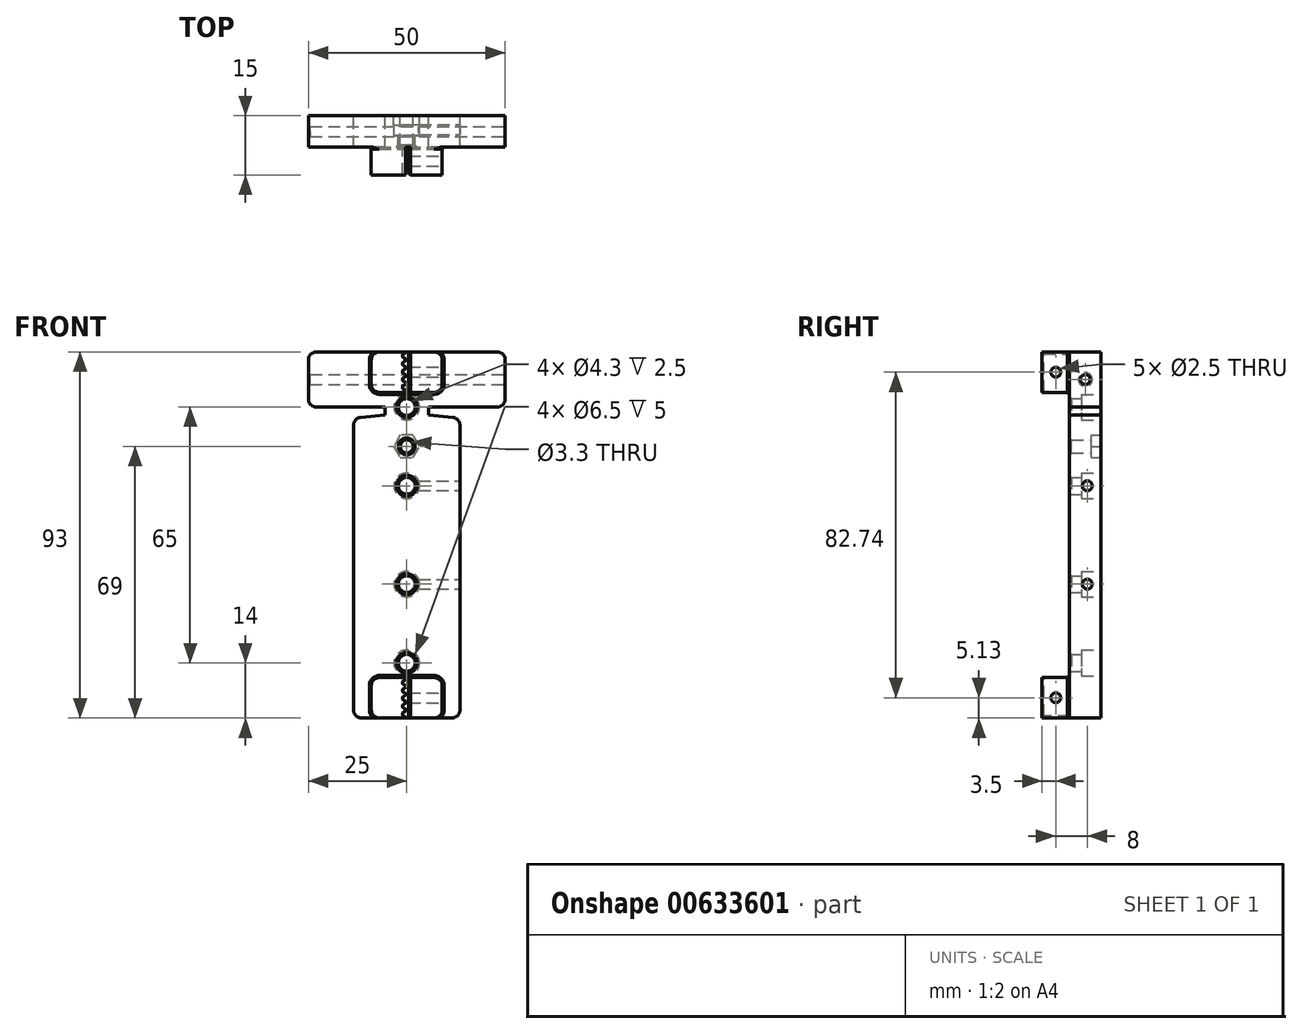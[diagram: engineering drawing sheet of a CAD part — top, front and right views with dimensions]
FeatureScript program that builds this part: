
annotation { "Feature Type Name" : "Feature", "Feature Type Description" : "" }
export const myFeature = defineFeature(function(context is Context, id is Id, definition is map)
    precondition{}
    {
        {
            var Q0;
            Q0=qCreatedBy(makeId("Front.planeOp"),FACE);
            var sketch = newSketch(context, id + "F0", { "sketchPlane" : qUnion([Q0])});
            skLineSegment(sketch, "E0.bottom", {"start": v(13.5, -86) * mm, "end": v(-13.5, -86) * mm});
            skLineSegment(sketch, "E0.left", {"start": v(13.5, -86) * mm, "end": v(13.5, -9.8) * mm});
            skLineSegment(sketch, "E0.right", {"start": v(-13.5, -86) * mm, "end": v(-13.5, -9.8) * mm});
            skLineSegment(sketch, "E1.top", {"start": v(-25, 7) * mm, "end": v(25, 7) * mm});
            skLineSegment(sketch, "E1.left", {"start": v(-25, -7) * mm, "end": v(-25, 7) * mm});
            skLineSegment(sketch, "E1.right", {"start": v(25, -7) * mm, "end": v(25, 7) * mm});
            skPoint(sketch, "E1.middle", {"position": v(0, 0) * mm});
            skCircle(sketch, "E2", {"center": v(0, -7) * mm, "radius": 2.15 * mm});
            skCircle(sketch, "E3", {"center": v(0, -17) * mm, "radius": 1.65 * mm});
            skCircle(sketch, "E4", {"center": v(0, -27) * mm, "radius": 2.15 * mm});
            skCircle(sketch, "E5", {"center": v(0, -52) * mm, "radius": 2.15 * mm});
            skCircle(sketch, "E6", {"center": v(0, -72) * mm, "radius": 2.15 * mm});
            skLineSegment(sketch, "E7", {"start": v(-32.04, -39.5) * mm, "end": v(39, -39.5) * mm, "construction": true});
            skLineSegment(sketch, "E8", {"start": v(-25, -7) * mm, "end": v(-13.5, -7) * mm});
            skLineSegment(sketch, "E9", {"start": v(13.5, -7) * mm, "end": v(25, -7) * mm});
            skLineSegment(sketch, "E10", {"start": v(0, 0) * mm, "end": v(0, -86) * mm, "construction": true});
            skLineSegment(sketch, "E11", {"start": v(-13.5, -7) * mm, "end": v(-5.5, -7) * mm});
            skLineSegment(sketch, "E12", {"start": v(-5.5, -7) * mm, "end": v(-5.5, -9) * mm});
            skLineSegment(sketch, "E13", {"start": v(-5.5, -9) * mm, "end": v(-13.5, -9.8) * mm});
            skLineSegment(sketch, "E14.MirrorCS", {"start": v(13.5, -7) * mm, "end": v(5.5, -7) * mm});
            skLineSegment(sketch, "E15.MirrorCS", {"start": v(5.5, -9) * mm, "end": v(13.5, -9.8) * mm});
            skLineSegment(sketch, "E16.MirrorCS", {"start": v(5.5, -7) * mm, "end": v(5.5, -9) * mm});
            skSolve(sketch);
        }
        {
            var Q0;
            Q0=makeQuery(id+"F0.imprint","IMPRINT",FACE,{"disambiguationData":[TD([[makeQuery(id+"F0.imprint","IMPRINT",EDGE,{"derivedFrom":sQuery(id+"F0.wireOp",EDGE,"E0.bottom")}),-1.0]])]});
            extrude(context, id + "F1", {"entities" : qUnion([Q0]), "endBound" : BoundingType.SYMMETRIC, "depth" : 8 * mm});
        }
        {
            var Q0;
            Q0=makeQuery(id+"F1.opExtrude","CAP_FACE",FACE,{"disambiguationData":[OSD([sQuery(id+"F0.wireOp",EDGE,"E0.bottom"),sQuery(id+"F0.wireOp",EDGE,"E0.left"),sQuery(id+"F0.wireOp",EDGE,"E0.right"),sQuery(id+"F0.wireOp",EDGE,"E1.top"),sQuery(id+"F0.wireOp",EDGE,"E1.left"),sQuery(id+"F0.wireOp",EDGE,"E1.right"),sQuery(id+"F0.wireOp",EDGE,"E2"),sQuery(id+"F0.wireOp",EDGE,"E3"),sQuery(id+"F0.wireOp",EDGE,"E4"),sQuery(id+"F0.wireOp",EDGE,"E5"),sQuery(id+"F0.wireOp",EDGE,"E6"),sQuery(id+"F0.wireOp",EDGE,"E8"),sQuery(id+"F0.wireOp",EDGE,"E9")])],"isStart":false});
            var sketch = newSketch(context, id + "F2", { "sketchPlane" : qUnion([Q0])});
            skLineSegment(sketch, "E17", {"start": v(0.48, 7) * mm, "end": v(0.48, 6) * mm});
            skLineSegment(sketch, "E18", {"start": v(-0.35, 7) * mm, "end": v(-0.35, 6.74) * mm});
            skArc(sketch, "E19", {"start": v(-0.35, 6.74) * mm, "mid": v(-0.4, 6.64) * mm, "end": v(-0.48, 6.6) * mm});
            skLineSegment(sketch, "E20", {"start": v(-1.63, 6) * mm, "end": v(0.48, 6) * mm, "construction": true});
            skArc(sketch, "E21", {"start": v(-1.1, 6) * mm, "mid": v(-1.02, 6.3) * mm, "end": v(-0.8, 6.5) * mm});
            skArc(sketch, "E22", {"start": v(-0.8, 6.5) * mm, "mid": v(-0.64, 6.56) * mm, "end": v(-0.48, 6.6) * mm});
            skArc(sketch, "E23.MirrorCS", {"start": v(-1.1, 6) * mm, "mid": v(-1.02, 5.7) * mm, "end": v(-0.8, 5.5) * mm});
            skArc(sketch, "E24.MirrorCS", {"start": v(-0.8, 5.5) * mm, "mid": v(-0.64, 5.44) * mm, "end": v(-0.48, 5.4) * mm});
            skArc(sketch, "E25.MirrorCS", {"start": v(-0.35, 5.26) * mm, "mid": v(-0.4, 5.36) * mm, "end": v(-0.48, 5.4) * mm});
            skLineSegment(sketch, "E26.MirrorCS", {"start": v(-0.35, 5) * mm, "end": v(-0.35, 5.26) * mm});
            skLineSegment(sketch, "E27.MirrorCS", {"start": v(0.48, 5) * mm, "end": v(0.48, 6) * mm});
            skLineSegment(sketch, "E28", {"start": v(-0.35, 5) * mm, "end": v(0.48, 5) * mm, "construction": true});
            skArc(sketch, "E29.MirrorCS", {"start": v(-0.35, 3.26) * mm, "mid": v(-0.4, 3.36) * mm, "end": v(-0.48, 3.4) * mm});
            skArc(sketch, "E30.MirrorCS", {"start": v(-0.8, 3.5) * mm, "mid": v(-0.64, 3.44) * mm, "end": v(-0.48, 3.4) * mm});
            skLineSegment(sketch, "E31.MirrorCS", {"start": v(-0.35, 5) * mm, "end": v(-0.35, 4.74) * mm});
            skArc(sketch, "E32.MirrorCS", {"start": v(-0.8, 4.5) * mm, "mid": v(-0.64, 4.56) * mm, "end": v(-0.48, 4.6) * mm});
            skArc(sketch, "E33.MirrorCS", {"start": v(-0.35, 4.74) * mm, "mid": v(-0.4, 4.64) * mm, "end": v(-0.48, 4.6) * mm});
            skLineSegment(sketch, "E34.MirrorCS", {"start": v(-0.35, 3) * mm, "end": v(-0.35, 3.26) * mm});
            skLineSegment(sketch, "E35.MirrorCS", {"start": v(-1.63, 4) * mm, "end": v(0.48, 4) * mm, "construction": true});
            skArc(sketch, "E36.MirrorCS", {"start": v(-1.1, 4) * mm, "mid": v(-1.02, 4.3) * mm, "end": v(-0.8, 4.5) * mm});
            skLineSegment(sketch, "E37.MirrorCS", {"start": v(0.48, 3) * mm, "end": v(0.48, 4) * mm});
            skArc(sketch, "E38.MirrorCS", {"start": v(-1.1, 4) * mm, "mid": v(-1.02, 3.7) * mm, "end": v(-0.8, 3.5) * mm});
            skLineSegment(sketch, "E39.MirrorCS", {"start": v(0.48, 5) * mm, "end": v(0.48, 4) * mm});
            skLineSegment(sketch, "E40", {"start": v(-0.35, 3) * mm, "end": v(0.48, 3) * mm, "construction": true});
            skLineSegment(sketch, "E41.MirrorCS", {"start": v(-0.35, 1) * mm, "end": v(-0.35, 0.74) * mm});
            skArc(sketch, "E42.MirrorCS", {"start": v(-0.35, -0.74) * mm, "mid": v(-0.4, -0.64) * mm, "end": v(-0.48, -0.6) * mm});
            skArc(sketch, "E43.MirrorCS", {"start": v(-0.35, 2.74) * mm, "mid": v(-0.4, 2.64) * mm, "end": v(-0.48, 2.6) * mm});
            skArc(sketch, "E44.MirrorCS", {"start": v(-0.35, 0.74) * mm, "mid": v(-0.4, 0.64) * mm, "end": v(-0.48, 0.6) * mm});
            skArc(sketch, "E45.MirrorCS", {"start": v(-0.8, -0.5) * mm, "mid": v(-0.64, -0.56) * mm, "end": v(-0.48, -0.6) * mm});
            skArc(sketch, "E46.MirrorCS", {"start": v(-0.35, 1.26) * mm, "mid": v(-0.4, 1.36) * mm, "end": v(-0.48, 1.4) * mm});
            skArc(sketch, "E47.MirrorCS", {"start": v(-0.8, 2.5) * mm, "mid": v(-0.64, 2.56) * mm, "end": v(-0.48, 2.6) * mm});
            skLineSegment(sketch, "E48.MirrorCS", {"start": v(-0.35, 3) * mm, "end": v(-0.35, 2.74) * mm});
            skLineSegment(sketch, "E49.MirrorCS", {"start": v(-0.35, 1) * mm, "end": v(-0.35, 1.26) * mm});
            skArc(sketch, "E50.MirrorCS", {"start": v(-0.8, 0.5) * mm, "mid": v(-0.64, 0.56) * mm, "end": v(-0.48, 0.6) * mm});
            skArc(sketch, "E51.MirrorCS", {"start": v(-0.8, 1.5) * mm, "mid": v(-0.64, 1.44) * mm, "end": v(-0.48, 1.4) * mm});
            skLineSegment(sketch, "E52.MirrorCS", {"start": v(-0.35, -1) * mm, "end": v(-0.35, -0.74) * mm});
            skArc(sketch, "E53.MirrorCS", {"start": v(-1.1, 0) * mm, "mid": v(-1.02, -0.3) * mm, "end": v(-0.8, -0.5) * mm});
            skLineSegment(sketch, "E54.MirrorCS", {"start": v(-1.63, 0) * mm, "end": v(0.48, 0) * mm, "construction": true});
            skLineSegment(sketch, "E55.MirrorCS", {"start": v(-0.35, 1) * mm, "end": v(0.48, 1) * mm, "construction": true});
            skLineSegment(sketch, "E56.MirrorCS", {"start": v(0.48, 1) * mm, "end": v(0.48, 2) * mm});
            skArc(sketch, "E57.MirrorCS", {"start": v(-1.1, 2) * mm, "mid": v(-1.02, 2.3) * mm, "end": v(-0.8, 2.5) * mm});
            skArc(sketch, "E58.MirrorCS", {"start": v(-1.1, 2) * mm, "mid": v(-1.02, 1.7) * mm, "end": v(-0.8, 1.5) * mm});
            skLineSegment(sketch, "E59.MirrorCS", {"start": v(0.48, 1) * mm, "end": v(0.48, 0) * mm});
            skArc(sketch, "E60.MirrorCS", {"start": v(-1.1, 0) * mm, "mid": v(-1.02, 0.3) * mm, "end": v(-0.8, 0.5) * mm});
            skLineSegment(sketch, "E61.MirrorCS", {"start": v(0.48, -1) * mm, "end": v(0.48, 0) * mm});
            skLineSegment(sketch, "E62.MirrorCS", {"start": v(0.48, 3) * mm, "end": v(0.48, 2) * mm});
            skLineSegment(sketch, "E63.MirrorCS", {"start": v(-1.63, 2) * mm, "end": v(0.48, 2) * mm, "construction": true});
            skLineSegment(sketch, "E64", {"start": v(-0.35, -1) * mm, "end": v(0.48, -1) * mm, "construction": true});
            skLineSegment(sketch, "E65.MirrorCS", {"start": v(-0.35, -3) * mm, "end": v(-0.35, -2.74) * mm});
            skArc(sketch, "E66.MirrorCS", {"start": v(-0.35, -1.26) * mm, "mid": v(-0.4, -1.36) * mm, "end": v(-0.48, -1.4) * mm});
            skArc(sketch, "E67.MirrorCS", {"start": v(-0.35, -2.74) * mm, "mid": v(-0.4, -2.64) * mm, "end": v(-0.48, -2.6) * mm});
            skLineSegment(sketch, "E68.MirrorCS", {"start": v(-0.35, -3) * mm, "end": v(-0.35, -3.26) * mm});
            skLineSegment(sketch, "E69.MirrorCS", {"start": v(-0.35, -1) * mm, "end": v(-0.35, -1.26) * mm});
            skArc(sketch, "E70.MirrorCS", {"start": v(-0.8, -2.5) * mm, "mid": v(-0.64, -2.56) * mm, "end": v(-0.48, -2.6) * mm});
            skArc(sketch, "E71.MirrorCS", {"start": v(-0.8, -1.5) * mm, "mid": v(-0.64, -1.44) * mm, "end": v(-0.48, -1.4) * mm});
            skLineSegment(sketch, "E72.MirrorCS", {"start": v(-0.35, -3) * mm, "end": v(0.48, -3) * mm, "construction": true});
            skLineSegment(sketch, "E73.MirrorCS", {"start": v(0.48, -3) * mm, "end": v(0.48, -2) * mm});
            skLineSegment(sketch, "E74.MirrorCS", {"start": v(-1.63, -2) * mm, "end": v(0.48, -2) * mm, "construction": true});
            skArc(sketch, "E75.MirrorCS", {"start": v(-1.1, -2) * mm, "mid": v(-1.02, -2.3) * mm, "end": v(-0.8, -2.5) * mm});
            skLineSegment(sketch, "E76.MirrorCS", {"start": v(0.48, -1) * mm, "end": v(0.48, -2) * mm});
            skArc(sketch, "E77.MirrorCS", {"start": v(-1.1, -2) * mm, "mid": v(-1.02, -1.7) * mm, "end": v(-0.8, -1.5) * mm});
            skLineSegment(sketch, "E78", {"start": v(0.48, 7) * mm, "end": v(9, 7) * mm});
            skLineSegment(sketch, "E79", {"start": v(9, 7) * mm, "end": v(9, -3.26) * mm});
            skLineSegment(sketch, "E80", {"start": v(9, -3.26) * mm, "end": v(0.48, -3.26) * mm});
            skLineSegment(sketch, "E81", {"start": v(-0.35, 7) * mm, "end": v(-9, 7) * mm});
            skLineSegment(sketch, "E82", {"start": v(-9, 7) * mm, "end": v(-9, -3.26) * mm});
            skLineSegment(sketch, "E83", {"start": v(-9, -3.26) * mm, "end": v(-0.35, -3.26) * mm});
            skLineSegment(sketch, "E84", {"start": v(0.48, -3) * mm, "end": v(0.48, -3.26) * mm});
            skLineSegment(sketch, "E85", {"start": v(-13.5, -39.5) * mm, "end": v(13.5, -39.5) * mm, "construction": true});
            skArc(sketch, "E86.MirrorCS", {"start": v(-0.35, -83.74) * mm, "mid": v(-0.4, -83.64) * mm, "end": v(-0.48, -83.6) * mm});
            skLineSegment(sketch, "E87.MirrorCS", {"start": v(-0.35, -84) * mm, "end": v(-0.35, -84.26) * mm});
            skArc(sketch, "E88.MirrorCS", {"start": v(-0.35, -84.26) * mm, "mid": v(-0.4, -84.36) * mm, "end": v(-0.48, -84.4) * mm});
            skArc(sketch, "E89.MirrorCS", {"start": v(-0.8, -83.5) * mm, "mid": v(-0.64, -83.56) * mm, "end": v(-0.48, -83.6) * mm});
            skLineSegment(sketch, "E90.MirrorCS", {"start": v(-0.35, -84) * mm, "end": v(-0.35, -83.74) * mm});
            skArc(sketch, "E91.MirrorCS", {"start": v(-0.8, -84.5) * mm, "mid": v(-0.64, -84.44) * mm, "end": v(-0.48, -84.4) * mm});
            skArc(sketch, "E92.MirrorCS", {"start": v(-0.35, -80.26) * mm, "mid": v(-0.4, -80.36) * mm, "end": v(-0.48, -80.4) * mm});
            skArc(sketch, "E93.MirrorCS", {"start": v(-0.35, -79.74) * mm, "mid": v(-0.4, -79.64) * mm, "end": v(-0.48, -79.6) * mm});
            skArc(sketch, "E94.MirrorCS", {"start": v(-0.8, -80.5) * mm, "mid": v(-0.64, -80.44) * mm, "end": v(-0.48, -80.4) * mm});
            skArc(sketch, "E95.MirrorCS", {"start": v(-0.8, -79.5) * mm, "mid": v(-0.64, -79.56) * mm, "end": v(-0.48, -79.6) * mm});
            skLineSegment(sketch, "E96.MirrorCS", {"start": v(-0.35, -80) * mm, "end": v(-0.35, -79.74) * mm});
            skLineSegment(sketch, "E97.MirrorCS", {"start": v(-0.35, -80) * mm, "end": v(-0.35, -80.26) * mm});
            skLineSegment(sketch, "E98.MirrorCS", {"start": v(-0.35, -78) * mm, "end": v(-0.35, -77.74) * mm});
            skLineSegment(sketch, "E99.MirrorCS", {"start": v(-0.35, -78) * mm, "end": v(-0.35, -78.26) * mm});
            skArc(sketch, "E100.MirrorCS", {"start": v(-0.35, -82.26) * mm, "mid": v(-0.4, -82.36) * mm, "end": v(-0.48, -82.4) * mm});
            skArc(sketch, "E101.MirrorCS", {"start": v(-0.8, -78.5) * mm, "mid": v(-0.64, -78.44) * mm, "end": v(-0.48, -78.4) * mm});
            skArc(sketch, "E102.MirrorCS", {"start": v(-0.35, -78.26) * mm, "mid": v(-0.4, -78.36) * mm, "end": v(-0.48, -78.4) * mm});
            skLineSegment(sketch, "E103.MirrorCS", {"start": v(-0.35, -82) * mm, "end": v(-0.35, -82.26) * mm});
            skArc(sketch, "E104.MirrorCS", {"start": v(-0.8, -82.5) * mm, "mid": v(-0.64, -82.44) * mm, "end": v(-0.48, -82.4) * mm});
            skArc(sketch, "E105.MirrorCS", {"start": v(-0.8, -85.5) * mm, "mid": v(-0.64, -85.56) * mm, "end": v(-0.48, -85.6) * mm});
            skArc(sketch, "E106.MirrorCS", {"start": v(-0.35, -77.74) * mm, "mid": v(-0.4, -77.64) * mm, "end": v(-0.48, -77.6) * mm});
            skArc(sketch, "E107.MirrorCS", {"start": v(-1.1, -83) * mm, "mid": v(-1.02, -83.3) * mm, "end": v(-0.8, -83.5) * mm});
            skArc(sketch, "E108.MirrorCS", {"start": v(-0.8, -77.5) * mm, "mid": v(-0.64, -77.56) * mm, "end": v(-0.48, -77.6) * mm});
            skLineSegment(sketch, "E109.MirrorCS", {"start": v(-0.35, -82) * mm, "end": v(-0.35, -81.74) * mm});
            skArc(sketch, "E110.MirrorCS", {"start": v(-0.8, -76.5) * mm, "mid": v(-0.64, -76.44) * mm, "end": v(-0.48, -76.4) * mm});
            skLineSegment(sketch, "E111.MirrorCS", {"start": v(0.48, -76) * mm, "end": v(0.48, -75.74) * mm});
            skLineSegment(sketch, "E112.MirrorCS", {"start": v(-0.35, -76) * mm, "end": v(-0.35, -75.74) * mm});
            skLineSegment(sketch, "E113.MirrorCS", {"start": v(-0.35, -84) * mm, "end": v(0.48, -84) * mm, "construction": true});
            skArc(sketch, "E114.MirrorCS", {"start": v(-0.8, -81.5) * mm, "mid": v(-0.64, -81.56) * mm, "end": v(-0.48, -81.6) * mm});
            skArc(sketch, "E115.MirrorCS", {"start": v(-1.1, -83) * mm, "mid": v(-1.02, -82.7) * mm, "end": v(-0.8, -82.5) * mm});
            skLineSegment(sketch, "E116.MirrorCS", {"start": v(-1.63, -83) * mm, "end": v(0.48, -83) * mm, "construction": true});
            skArc(sketch, "E117.MirrorCS", {"start": v(-0.35, -85.74) * mm, "mid": v(-0.4, -85.64) * mm, "end": v(-0.48, -85.6) * mm});
            skArc(sketch, "E118.MirrorCS", {"start": v(-1.1, -85) * mm, "mid": v(-1.02, -85.3) * mm, "end": v(-0.8, -85.5) * mm});
            skArc(sketch, "E119.MirrorCS", {"start": v(-1.1, -81) * mm, "mid": v(-1.02, -80.7) * mm, "end": v(-0.8, -80.5) * mm});
            skArc(sketch, "E120.MirrorCS", {"start": v(-1.1, -85) * mm, "mid": v(-1.02, -84.7) * mm, "end": v(-0.8, -84.5) * mm});
            skLineSegment(sketch, "E121.MirrorCS", {"start": v(-0.35, -76) * mm, "end": v(-0.35, -76.26) * mm});
            skLineSegment(sketch, "E122.MirrorCS", {"start": v(-0.35, -86) * mm, "end": v(-0.35, -85.74) * mm});
            skLineSegment(sketch, "E123.MirrorCS", {"start": v(-0.35, -76) * mm, "end": v(0.48, -76) * mm, "construction": true});
            skArc(sketch, "E124.MirrorCS", {"start": v(-0.35, -81.74) * mm, "mid": v(-0.4, -81.64) * mm, "end": v(-0.48, -81.6) * mm});
            skLineSegment(sketch, "E125.MirrorCS", {"start": v(0.48, -84) * mm, "end": v(0.48, -85) * mm});
            skArc(sketch, "E126.MirrorCS", {"start": v(-1.1, -77) * mm, "mid": v(-1.02, -77.3) * mm, "end": v(-0.8, -77.5) * mm});
            skArc(sketch, "E127.MirrorCS", {"start": v(-0.35, -76.26) * mm, "mid": v(-0.4, -76.36) * mm, "end": v(-0.48, -76.4) * mm});
            skArc(sketch, "E128.MirrorCS", {"start": v(-1.1, -77) * mm, "mid": v(-1.02, -76.7) * mm, "end": v(-0.8, -76.5) * mm});
            skLineSegment(sketch, "E129.MirrorCS", {"start": v(0.48, -84) * mm, "end": v(0.48, -83) * mm});
            skArc(sketch, "E130.MirrorCS", {"start": v(-1.1, -79) * mm, "mid": v(-1.02, -79.3) * mm, "end": v(-0.8, -79.5) * mm});
            skLineSegment(sketch, "E131.MirrorCS", {"start": v(0.48, -82) * mm, "end": v(0.48, -83) * mm});
            skArc(sketch, "E132.MirrorCS", {"start": v(-1.1, -79) * mm, "mid": v(-1.02, -78.7) * mm, "end": v(-0.8, -78.5) * mm});
            skLineSegment(sketch, "E133.MirrorCS", {"start": v(0.48, -82) * mm, "end": v(0.48, -81) * mm});
            skLineSegment(sketch, "E134.MirrorCS", {"start": v(-0.35, -80) * mm, "end": v(0.48, -80) * mm, "construction": true});
            skLineSegment(sketch, "E135.MirrorCS", {"start": v(0.48, -78) * mm, "end": v(0.48, -77) * mm});
            skLineSegment(sketch, "E136.MirrorCS", {"start": v(0.48, -76) * mm, "end": v(0.48, -77) * mm});
            skLineSegment(sketch, "E137.MirrorCS", {"start": v(0.48, -80) * mm, "end": v(0.48, -79) * mm});
            skLineSegment(sketch, "E138.MirrorCS", {"start": v(-1.63, -85) * mm, "end": v(0.48, -85) * mm, "construction": true});
            skLineSegment(sketch, "E139.MirrorCS", {"start": v(-0.35, -78) * mm, "end": v(0.48, -78) * mm, "construction": true});
            skArc(sketch, "E140.MirrorCS", {"start": v(-1.1, -81) * mm, "mid": v(-1.02, -81.3) * mm, "end": v(-0.8, -81.5) * mm});
            skLineSegment(sketch, "E141.MirrorCS", {"start": v(0.48, -86) * mm, "end": v(0.48, -85) * mm});
            skLineSegment(sketch, "E142.MirrorCS", {"start": v(0.48, -80) * mm, "end": v(0.48, -81) * mm});
            skLineSegment(sketch, "E143.MirrorCS", {"start": v(0.48, -78) * mm, "end": v(0.48, -79) * mm});
            skLineSegment(sketch, "E144.MirrorCS", {"start": v(-0.35, -82) * mm, "end": v(0.48, -82) * mm, "construction": true});
            skLineSegment(sketch, "E145.MirrorCS", {"start": v(-1.63, -79) * mm, "end": v(0.48, -79) * mm, "construction": true});
            skLineSegment(sketch, "E146.MirrorCS", {"start": v(-1.63, -81) * mm, "end": v(0.48, -81) * mm, "construction": true});
            skLineSegment(sketch, "E147.MirrorCS", {"start": v(-1.63, -77) * mm, "end": v(0.48, -77) * mm, "construction": true});
            skLineSegment(sketch, "E148.MirrorCS", {"start": v(9, -86) * mm, "end": v(9, -75.74) * mm});
            skLineSegment(sketch, "E149.MirrorCS", {"start": v(0.48, -86) * mm, "end": v(9, -86) * mm});
            skLineSegment(sketch, "E150.MirrorCS", {"start": v(-9, -86) * mm, "end": v(-9, -75.74) * mm});
            skLineSegment(sketch, "E151.MirrorCS", {"start": v(-0.35, -86) * mm, "end": v(-9, -86) * mm});
            skLineSegment(sketch, "E152.MirrorCS", {"start": v(9, -75.74) * mm, "end": v(0.48, -75.74) * mm});
            skLineSegment(sketch, "E153.MirrorCS", {"start": v(-9, -75.74) * mm, "end": v(-0.35, -75.74) * mm});
            skSolve(sketch);
        }
        {
            var Q0;
            Q0=qSketchRegion(id+"F2",true);
            extrude(context, id + "F3", {"entities" : qUnion([Q0]), "operationType" : NewBodyOperationType.ADD, "depth" : 7 * mm});
        }
        {
            var Q0;
            Q0=makeQuery(id+"F1.opExtrude","SWEPT_FACE",FACE,{"disambiguationData":[OSD([sQuery(id+"F0.wireOp",EDGE,"E1.right")])]});
            var sketch = newSketch(context, id + "F4", { "sketchPlane" : qUnion([Q0])});
            skCircle(sketch, "E154", {"center": v(0, 0) * mm, "radius": 1.25 * mm});
            skSolve(sketch);
        }
        {
            var Q0;
            Q0=qSketchRegion(id+"F4",true);
            extrude(context, id + "F5", {"entities" : qUnion([Q0]), "operationType" : NewBodyOperationType.REMOVE, "endBound" : BoundingType.THROUGH_ALL, "oppositeDirection" : true, "depth" : 25 * mm});
        }
        {
            var Q0;
            Q0=makeQuery(id+"F1.opExtrude","SWEPT_FACE",FACE,{"disambiguationData":[OSD([sQuery(id+"F0.wireOp",EDGE,"E0.left")])]});
            var sketch = newSketch(context, id + "F6", { "sketchPlane" : qUnion([Q0])});
            skLineSegment(sketch, "E155.0", {"start": v(-4, -29.15) * mm, "end": v(-4, -24.85) * mm, "construction": true});
            skLineSegment(sketch, "E156.0", {"start": v(-4, -54.15) * mm, "end": v(-4, -49.85) * mm, "construction": true});
            skLineSegment(sketch, "E157", {"start": v(-4, -27) * mm, "end": v(4, -27) * mm, "construction": true});
            skLineSegment(sketch, "E158", {"start": v(-4, -52) * mm, "end": v(4, -52) * mm, "construction": true});
            skPoint(sketch, "E159.centerSnap0", {"position": v(0, -27) * mm});
            skPoint(sketch, "E160.centerSnap0", {"position": v(0, -52) * mm});
            skLineSegment(sketch, "E161", {"start": v(0.5, -27) * mm, "end": v(0.5, -52) * mm, "construction": true});
            skCircle(sketch, "E162", {"center": v(0.5, -27) * mm, "radius": 1.25 * mm});
            skCircle(sketch, "E163", {"center": v(0.5, -52) * mm, "radius": 1.25 * mm});
            skSolve(sketch);
        }
        {
            var Q0;
            Q0=qSketchRegion(id+"F6",true);
            extrude(context, id + "F7", {"entities" : qUnion([Q0]), "operationType" : NewBodyOperationType.REMOVE, "oppositeDirection" : true, "depth" : 13.5 * mm});
        }
        {
            var Q0;
            Q0=makeQuery(id+"F1.opExtrude","CAP_FACE",FACE,{"disambiguationData":[OSD([sQuery(id+"F0.wireOp",EDGE,"E0.bottom"),sQuery(id+"F0.wireOp",EDGE,"E0.left"),sQuery(id+"F0.wireOp",EDGE,"E0.right"),sQuery(id+"F0.wireOp",EDGE,"E1.top"),sQuery(id+"F0.wireOp",EDGE,"E1.left"),sQuery(id+"F0.wireOp",EDGE,"E1.right"),sQuery(id+"F0.wireOp",EDGE,"E2"),sQuery(id+"F0.wireOp",EDGE,"E3"),sQuery(id+"F0.wireOp",EDGE,"E4"),sQuery(id+"F0.wireOp",EDGE,"E5"),sQuery(id+"F0.wireOp",EDGE,"E6"),sQuery(id+"F0.wireOp",EDGE,"E8"),sQuery(id+"F0.wireOp",EDGE,"E9")])],"isStart":true});
            var sketch = newSketch(context, id + "F8", { "sketchPlane" : qUnion([Q0])});
            skCircle(sketch, "E164", {"center": v(0, -7) * mm, "radius": 3.25 * mm});
            skCircle(sketch, "E165", {"center": v(0, -27) * mm, "radius": 3.25 * mm});
            skCircle(sketch, "E166", {"center": v(0, -52) * mm, "radius": 3.25 * mm});
            skCircle(sketch, "E167", {"center": v(0, -72) * mm, "radius": 3.25 * mm});
            skSolve(sketch);
        }
        {
            var Q0;
            Q0=qSketchRegion(id+"F8",true);
            extrude(context, id + "F9", {"entities" : qUnion([Q0]), "operationType" : NewBodyOperationType.REMOVE, "oppositeDirection" : true, "depth" : 5 * mm});
        }
        {
            var Q0;
            Q0=makeQuery(id+"F1.opExtrude","CAP_FACE",FACE,{"disambiguationData":[OSD([sQuery(id+"F0.wireOp",EDGE,"E0.bottom"),sQuery(id+"F0.wireOp",EDGE,"E0.left"),sQuery(id+"F0.wireOp",EDGE,"E0.right"),sQuery(id+"F0.wireOp",EDGE,"E1.top"),sQuery(id+"F0.wireOp",EDGE,"E1.left"),sQuery(id+"F0.wireOp",EDGE,"E1.right"),sQuery(id+"F0.wireOp",EDGE,"E2"),sQuery(id+"F0.wireOp",EDGE,"E3"),sQuery(id+"F0.wireOp",EDGE,"E4"),sQuery(id+"F0.wireOp",EDGE,"E5"),sQuery(id+"F0.wireOp",EDGE,"E6"),sQuery(id+"F0.wireOp",EDGE,"E8"),sQuery(id+"F0.wireOp",EDGE,"E9")])],"isStart":true});
            var sketch = newSketch(context, id + "F10", { "sketchPlane" : qUnion([Q0])});
            skCircle(sketch, "E168.cCircle", {"center": v(0, -17) * mm, "radius": 3.3 * mm, "construction": true});
            skLineSegment(sketch, "E168.0", {"start": v(-3.3, -17) * mm, "end": v(-1.65, -14.15) * mm});
            skLineSegment(sketch, "E168.1", {"start": v(-1.65, -14.15) * mm, "end": v(1.65, -14.15) * mm});
            skLineSegment(sketch, "E168.2", {"start": v(1.65, -14.15) * mm, "end": v(3.3, -17) * mm});
            skLineSegment(sketch, "E168.3", {"start": v(3.3, -17) * mm, "end": v(1.65, -19.85) * mm});
            skLineSegment(sketch, "E168.4", {"start": v(1.65, -19.85) * mm, "end": v(-1.65, -19.85) * mm});
            skLineSegment(sketch, "E168.5", {"start": v(-1.65, -19.85) * mm, "end": v(-3.3, -17) * mm});
            skSolve(sketch);
        }
        {
            var Q0;
            Q0=makeQuery(id+"F10.imprint","IMPRINT",FACE,{"disambiguationData":[TD([[makeQuery(id+"F10.imprint","IMPRINT",EDGE,{"derivedFrom":sQuery(id+"F10.wireOp",EDGE,"E168.0")}),-1.0]])]});
            extrude(context, id + "F11", {"entities" : qUnion([Q0]), "operationType" : NewBodyOperationType.REMOVE, "oppositeDirection" : true, "depth" : 2.4 * mm});
        }
        {
            var Q0;
            Q0=makeQuery(id+"F1.opExtrude","SWEPT_EDGE",EDGE,{"disambiguationData":[OSD([sQuery(id+"F0.wireOp",EDGE,"E0.bottom"),sQuery(id+"F0.wireOp",EDGE,"E0.right")])]});
            var Q1;
            Q1=makeQuery(id+"F1.opExtrude","SWEPT_EDGE",EDGE,{"disambiguationData":[OSD([sQuery(id+"F0.wireOp",EDGE,"E0.bottom"),sQuery(id+"F0.wireOp",EDGE,"E0.left")])]});
            var Q2;
            Q2=makeQuery(id+"F3.opExtrude","SWEPT_EDGE",EDGE,{"disambiguationData":[OSD([sQuery(id+"F0.wireOp",EDGE,"E0.bottom"),sQuery(id+"F2.wireOp",EDGE,"E148.MirrorCS"),sQuery(id+"F2.wireOp",EDGE,"E149.MirrorCS")])]});
            var Q3;
            Q3=makeQuery(id+"F3.opExtrude","SWEPT_EDGE",EDGE,{"disambiguationData":[OSD([sQuery(id+"F0.wireOp",EDGE,"E0.bottom"),sQuery(id+"F2.wireOp",EDGE,"E150.MirrorCS"),sQuery(id+"F2.wireOp",EDGE,"E151.MirrorCS")])]});
            var Q4;
            Q4=makeQuery(id+"F3.opExtrude","SWEPT_EDGE",EDGE,{"disambiguationData":[OSD([sQuery(id+"F2.wireOp",EDGE,"E79"),sQuery(id+"F2.wireOp",EDGE,"E80")])]});
            var Q5;
            Q5=makeQuery(id+"F3.opExtrude","SWEPT_EDGE",EDGE,{"disambiguationData":[OSD([sQuery(id+"F2.wireOp",EDGE,"E82"),sQuery(id+"F2.wireOp",EDGE,"E83")])]});
            var Q6;
            Q6=makeQuery(id+"F1.opExtrude","SWEPT_EDGE",EDGE,{"disambiguationData":[OSD([sQuery(id+"F0.wireOp",EDGE,"E1.right"),sQuery(id+"F0.wireOp",EDGE,"E9")])]});
            var Q7;
            Q7=makeQuery(id+"F1.opExtrude","SWEPT_EDGE",EDGE,{"disambiguationData":[OSD([sQuery(id+"F0.wireOp",EDGE,"E0.left"),sQuery(id+"F0.wireOp",EDGE,"E9")])]});
            var Q8;
            Q8=makeQuery(id+"F3.opExtrude","SWEPT_EDGE",EDGE,{"disambiguationData":[OSD([sQuery(id+"F2.wireOp",EDGE,"E148.MirrorCS"),sQuery(id+"F2.wireOp",EDGE,"E152.MirrorCS")])]});
            var Q9;
            Q9=makeQuery(id+"F3.opExtrude","SWEPT_EDGE",EDGE,{"disambiguationData":[OSD([sQuery(id+"F2.wireOp",EDGE,"E150.MirrorCS"),sQuery(id+"F2.wireOp",EDGE,"E153.MirrorCS")])]});
            var Q10;
            Q10=makeQuery(id+"F1.opExtrude","SWEPT_EDGE",EDGE,{"disambiguationData":[OSD([sQuery(id+"F0.wireOp",EDGE,"E0.right"),sQuery(id+"F0.wireOp",EDGE,"E8")])]});
            var Q11;
            Q11=makeQuery(id+"F1.opExtrude","SWEPT_EDGE",EDGE,{"disambiguationData":[OSD([sQuery(id+"F0.wireOp",EDGE,"E1.left"),sQuery(id+"F0.wireOp",EDGE,"E8")])]});
            var Q12;
            Q12=makeQuery(id+"F1.opExtrude","SWEPT_EDGE",EDGE,{"disambiguationData":[OSD([sQuery(id+"F0.wireOp",EDGE,"E1.top"),sQuery(id+"F0.wireOp",EDGE,"E1.left")])]});
            var Q13;
            Q13=makeQuery(id+"F1.opExtrude","SWEPT_EDGE",EDGE,{"disambiguationData":[OSD([sQuery(id+"F0.wireOp",EDGE,"E1.top"),sQuery(id+"F0.wireOp",EDGE,"E1.right")])]});
            var Q14;
            Q14=makeQuery(id+"F3.opExtrude","SWEPT_EDGE",EDGE,{"disambiguationData":[OSD([sQuery(id+"F0.wireOp",EDGE,"E1.top"),sQuery(id+"F2.wireOp",EDGE,"E78"),sQuery(id+"F2.wireOp",EDGE,"E79")])]});
            var Q15;
            Q15=makeQuery(id+"F3.opExtrude","SWEPT_EDGE",EDGE,{"disambiguationData":[OSD([sQuery(id+"F0.wireOp",EDGE,"E1.top"),sQuery(id+"F2.wireOp",EDGE,"E81"),sQuery(id+"F2.wireOp",EDGE,"E82")])]});
            fillet(context, id + "F12", {"entities" : qUnion([Q0, Q1, Q2, Q3, Q4, Q5, Q6, Q7, Q8, Q9, Q10, Q11, Q12, Q13, Q14, Q15]), "radius" : 2 * mm, "tangentPropagation" : true, "allowEdgeOverflow" : false});
        }
        {
            var Q0;
            Q0=makeQuery(id+"F3.opExtrude","SWEPT_FACE",FACE,{"disambiguationData":[OSD([sQuery(id+"F2.wireOp",EDGE,"E79")])]});
            var sketch = newSketch(context, id + "F13", { "sketchPlane" : qUnion([Q0])});
            skCircle(sketch, "E169", {"center": v(-7.5, 1.87) * mm, "radius": 1.25 * mm});
            skCircle(sketch, "E170", {"center": v(-7.5, -80.87) * mm, "radius": 1.25 * mm});
            skSolve(sketch);
        }
        {
            var Q0;
            Q0=makeQuery(id+"F13.imprint","IMPRINT",FACE,{"disambiguationData":[TD([[makeQuery(id+"F13.imprint","IMPRINT",EDGE,{"derivedFrom":sQuery(id+"F13.wireOp",EDGE,"E169")}),1.0]])]});
            var Q1;
            Q1=makeQuery(id+"F13.imprint","IMPRINT",FACE,{"disambiguationData":[TD([[makeQuery(id+"F13.imprint","IMPRINT",EDGE,{"derivedFrom":sQuery(id+"F13.wireOp",EDGE,"E170")}),1.0]])]});
            extrude(context, id + "F14", {"entities" : qUnion([Q0, Q1]), "operationType" : NewBodyOperationType.REMOVE, "endBound" : BoundingType.UP_TO_NEXT, "oppositeDirection" : true, "depth" : 25 * mm, "offsetDistance" : 25 * mm});
        }
        {
            var Q0;
            Q0=makeQuery(id+"F5.boolean.opBoolean","INTERSECT",EDGE,{"derivedFrom":[makeQuery(id+"F1.opExtrude","SWEPT_FACE",FACE,{"disambiguationData":[OSD([sQuery(id+"F0.wireOp",EDGE,"E1.left")])]}),makeQuery(id+"F5.opExtrude","SWEPT_FACE",FACE,{"disambiguationData":[OSD([sQuery(id+"F4.wireOp",EDGE,"E154")])]})]});
            var Q1;
            Q1=makeQuery(id+"F5.boolean.opBoolean","COPY",EDGE,{"derivedFrom":makeQuery(id+"F5.opExtrude","CAP_EDGE",EDGE,{"disambiguationData":[OSD([sQuery(id+"F4.wireOp",EDGE,"E154")])],"isStart":true})});
            var Q2;
            Q2=makeQuery(id+"F14.boolean.opBoolean","COPY",EDGE,{"derivedFrom":makeQuery(id+"F14.opExtrude","CAP_EDGE",EDGE,{"disambiguationData":[OSD([sQuery(id+"F13.wireOp",EDGE,"E169")])],"isStart":true})});
            var Q3;
            Q3=makeQuery(id+"F7.boolean.opBoolean","COPY",EDGE,{"derivedFrom":makeQuery(id+"F7.opExtrude","CAP_EDGE",EDGE,{"disambiguationData":[OSD([sQuery(id+"F6.wireOp",EDGE,"E162")])],"isStart":true})});
            var Q4;
            Q4=makeQuery(id+"F7.boolean.opBoolean","COPY",EDGE,{"derivedFrom":makeQuery(id+"F7.opExtrude","CAP_EDGE",EDGE,{"disambiguationData":[OSD([sQuery(id+"F6.wireOp",EDGE,"E163")])],"isStart":true})});
            var Q5;
            Q5=makeQuery(id+"F14.boolean.opBoolean","COPY",EDGE,{"derivedFrom":makeQuery(id+"F14.opExtrude","CAP_EDGE",EDGE,{"disambiguationData":[OSD([sQuery(id+"F13.wireOp",EDGE,"E170")])],"isStart":true})});
            var Q6;
            Q6=makeQuery(id+"F3.opExtrude","CAP_EDGE",EDGE,{"disambiguationData":[OSD([sQuery(id+"F2.wireOp",EDGE,"E17"),sQuery(id+"F2.wireOp",EDGE,"E27.MirrorCS"),sQuery(id+"F2.wireOp",EDGE,"E37.MirrorCS"),sQuery(id+"F2.wireOp",EDGE,"E39.MirrorCS"),sQuery(id+"F2.wireOp",EDGE,"E56.MirrorCS"),sQuery(id+"F2.wireOp",EDGE,"E59.MirrorCS"),sQuery(id+"F2.wireOp",EDGE,"E61.MirrorCS"),sQuery(id+"F2.wireOp",EDGE,"E62.MirrorCS"),sQuery(id+"F2.wireOp",EDGE,"E73.MirrorCS"),sQuery(id+"F2.wireOp",EDGE,"E76.MirrorCS"),sQuery(id+"F2.wireOp",EDGE,"E84")])],"isStart":false});
            var Q7;
            Q7=makeQuery(id+"F3.opExtrude","SWEPT_EDGE",EDGE,{"disambiguationData":[OSD([sQuery(id+"F0.wireOp",EDGE,"E1.top"),sQuery(id+"F2.wireOp",EDGE,"E17"),sQuery(id+"F2.wireOp",EDGE,"E78")])]});
            var Q8;
            Q8=makeQuery(id+"F14.boolean.opBoolean","COPY",EDGE,{"derivedFrom":makeQuery(id+"F14.opExtrude","CAP_EDGE",EDGE,{"disambiguationData":[OSD([sQuery(id+"F13.wireOp",EDGE,"E169")])],"isStart":false})});
            var Q9;
            Q9=makeQuery(id+"F3.opExtrude","SWEPT_EDGE",EDGE,{"disambiguationData":[OSD([sQuery(id+"F0.wireOp",EDGE,"E0.bottom"),sQuery(id+"F2.wireOp",EDGE,"E141.MirrorCS"),sQuery(id+"F2.wireOp",EDGE,"E149.MirrorCS")])]});
            var Q10;
            Q10=makeQuery(id+"F14.boolean.opBoolean","COPY",EDGE,{"derivedFrom":makeQuery(id+"F14.opExtrude","CAP_EDGE",EDGE,{"disambiguationData":[OSD([sQuery(id+"F13.wireOp",EDGE,"E170")])],"isStart":false})});
            var Q11;
            Q11=makeQuery(id+"F3.opExtrude","CAP_EDGE",EDGE,{"disambiguationData":[OSD([sQuery(id+"F2.wireOp",EDGE,"E111.MirrorCS"),sQuery(id+"F2.wireOp",EDGE,"E125.MirrorCS"),sQuery(id+"F2.wireOp",EDGE,"E129.MirrorCS"),sQuery(id+"F2.wireOp",EDGE,"E131.MirrorCS"),sQuery(id+"F2.wireOp",EDGE,"E133.MirrorCS"),sQuery(id+"F2.wireOp",EDGE,"E135.MirrorCS"),sQuery(id+"F2.wireOp",EDGE,"E136.MirrorCS"),sQuery(id+"F2.wireOp",EDGE,"E137.MirrorCS"),sQuery(id+"F2.wireOp",EDGE,"E141.MirrorCS"),sQuery(id+"F2.wireOp",EDGE,"E142.MirrorCS"),sQuery(id+"F2.wireOp",EDGE,"E143.MirrorCS")])],"isStart":false});
            var Q12;
            Q12=makeQuery(id+"F1.opExtrude","CAP_EDGE",EDGE,{"disambiguationData":[OSD([sQuery(id+"F0.wireOp",EDGE,"E2")])],"isStart":false});
            var Q13;
            Q13=makeQuery(id+"F1.opExtrude","CAP_EDGE",EDGE,{"disambiguationData":[OSD([sQuery(id+"F0.wireOp",EDGE,"E3")])],"isStart":false});
            var Q14;
            Q14=makeQuery(id+"F1.opExtrude","CAP_EDGE",EDGE,{"disambiguationData":[OSD([sQuery(id+"F0.wireOp",EDGE,"E4")])],"isStart":false});
            var Q15;
            Q15=makeQuery(id+"F1.opExtrude","CAP_EDGE",EDGE,{"disambiguationData":[OSD([sQuery(id+"F0.wireOp",EDGE,"E5")])],"isStart":false});
            var Q16;
            Q16=makeQuery(id+"F1.opExtrude","CAP_EDGE",EDGE,{"disambiguationData":[OSD([sQuery(id+"F0.wireOp",EDGE,"E6")])],"isStart":false});
            var Q17;
            {var subQ0=sQuery(id+"F0.wireOp",EDGE,"E1.top");Q17=makeQuery(id+"F12.opFillet","BLEND_EDGE",EDGE,{"blendedFrom":[makeQuery(id+"F3.opExtrude","SWEPT_EDGE",EDGE,{"disambiguationData":[OSD([subQ0,sQuery(id+"F2.wireOp",EDGE,"E78"),sQuery(id+"F2.wireOp",EDGE,"E79")])]}),makeQuery(id+"F1.opExtrude","CAP_FACE",FACE,{"disambiguationData":[OSD([sQuery(id+"F0.wireOp",EDGE,"E0.bottom"),sQuery(id+"F0.wireOp",EDGE,"E0.left"),sQuery(id+"F0.wireOp",EDGE,"E0.right"),subQ0,sQuery(id+"F0.wireOp",EDGE,"E1.left"),sQuery(id+"F0.wireOp",EDGE,"E1.right"),sQuery(id+"F0.wireOp",EDGE,"E2"),sQuery(id+"F0.wireOp",EDGE,"E3"),sQuery(id+"F0.wireOp",EDGE,"E4"),sQuery(id+"F0.wireOp",EDGE,"E5"),sQuery(id+"F0.wireOp",EDGE,"E6"),sQuery(id+"F0.wireOp",EDGE,"E8"),sQuery(id+"F0.wireOp",EDGE,"E9")])],"isStart":false})],"blendedInto":[makeQuery(id+"F1.opExtrude","CAP_FACE",FACE,{"disambiguationData":[OSD([sQuery(id+"F0.wireOp",EDGE,"E0.bottom"),sQuery(id+"F0.wireOp",EDGE,"E0.left"),sQuery(id+"F0.wireOp",EDGE,"E0.right"),subQ0,sQuery(id+"F0.wireOp",EDGE,"E1.left"),sQuery(id+"F0.wireOp",EDGE,"E1.right"),sQuery(id+"F0.wireOp",EDGE,"E2"),sQuery(id+"F0.wireOp",EDGE,"E3"),sQuery(id+"F0.wireOp",EDGE,"E4"),sQuery(id+"F0.wireOp",EDGE,"E5"),sQuery(id+"F0.wireOp",EDGE,"E6"),sQuery(id+"F0.wireOp",EDGE,"E8"),sQuery(id+"F0.wireOp",EDGE,"E9")])],"isStart":false})]});}
            var Q18;
            Q18=makeQuery(id+"F12.opFillet","BLEND_EDGE",EDGE,{"blendedFrom":[makeQuery(id+"F3.opExtrude","SWEPT_EDGE",EDGE,{"disambiguationData":[OSD([sQuery(id+"F2.wireOp",EDGE,"E82"),sQuery(id+"F2.wireOp",EDGE,"E83")])]}),makeQuery(id+"F1.opExtrude","CAP_FACE",FACE,{"disambiguationData":[OSD([sQuery(id+"F0.wireOp",EDGE,"E0.bottom"),sQuery(id+"F0.wireOp",EDGE,"E0.left"),sQuery(id+"F0.wireOp",EDGE,"E0.right"),sQuery(id+"F0.wireOp",EDGE,"E1.top"),sQuery(id+"F0.wireOp",EDGE,"E1.left"),sQuery(id+"F0.wireOp",EDGE,"E1.right"),sQuery(id+"F0.wireOp",EDGE,"E2"),sQuery(id+"F0.wireOp",EDGE,"E3"),sQuery(id+"F0.wireOp",EDGE,"E4"),sQuery(id+"F0.wireOp",EDGE,"E5"),sQuery(id+"F0.wireOp",EDGE,"E6"),sQuery(id+"F0.wireOp",EDGE,"E8"),sQuery(id+"F0.wireOp",EDGE,"E9")])],"isStart":false})],"blendedInto":[makeQuery(id+"F1.opExtrude","CAP_FACE",FACE,{"disambiguationData":[OSD([sQuery(id+"F0.wireOp",EDGE,"E0.bottom"),sQuery(id+"F0.wireOp",EDGE,"E0.left"),sQuery(id+"F0.wireOp",EDGE,"E0.right"),sQuery(id+"F0.wireOp",EDGE,"E1.top"),sQuery(id+"F0.wireOp",EDGE,"E1.left"),sQuery(id+"F0.wireOp",EDGE,"E1.right"),sQuery(id+"F0.wireOp",EDGE,"E2"),sQuery(id+"F0.wireOp",EDGE,"E3"),sQuery(id+"F0.wireOp",EDGE,"E4"),sQuery(id+"F0.wireOp",EDGE,"E5"),sQuery(id+"F0.wireOp",EDGE,"E6"),sQuery(id+"F0.wireOp",EDGE,"E8"),sQuery(id+"F0.wireOp",EDGE,"E9")])],"isStart":false})]});
            var Q19;
            Q19=makeQuery(id+"F12.opFillet","BLEND_EDGE",EDGE,{"blendedFrom":[makeQuery(id+"F3.opExtrude","SWEPT_EDGE",EDGE,{"disambiguationData":[OSD([sQuery(id+"F2.wireOp",EDGE,"E150.MirrorCS"),sQuery(id+"F2.wireOp",EDGE,"E153.MirrorCS")])]}),makeQuery(id+"F1.opExtrude","CAP_FACE",FACE,{"disambiguationData":[OSD([sQuery(id+"F0.wireOp",EDGE,"E0.bottom"),sQuery(id+"F0.wireOp",EDGE,"E0.left"),sQuery(id+"F0.wireOp",EDGE,"E0.right"),sQuery(id+"F0.wireOp",EDGE,"E1.top"),sQuery(id+"F0.wireOp",EDGE,"E1.left"),sQuery(id+"F0.wireOp",EDGE,"E1.right"),sQuery(id+"F0.wireOp",EDGE,"E2"),sQuery(id+"F0.wireOp",EDGE,"E3"),sQuery(id+"F0.wireOp",EDGE,"E4"),sQuery(id+"F0.wireOp",EDGE,"E5"),sQuery(id+"F0.wireOp",EDGE,"E6"),sQuery(id+"F0.wireOp",EDGE,"E8"),sQuery(id+"F0.wireOp",EDGE,"E9")])],"isStart":false})],"blendedInto":[makeQuery(id+"F1.opExtrude","CAP_FACE",FACE,{"disambiguationData":[OSD([sQuery(id+"F0.wireOp",EDGE,"E0.bottom"),sQuery(id+"F0.wireOp",EDGE,"E0.left"),sQuery(id+"F0.wireOp",EDGE,"E0.right"),sQuery(id+"F0.wireOp",EDGE,"E1.top"),sQuery(id+"F0.wireOp",EDGE,"E1.left"),sQuery(id+"F0.wireOp",EDGE,"E1.right"),sQuery(id+"F0.wireOp",EDGE,"E2"),sQuery(id+"F0.wireOp",EDGE,"E3"),sQuery(id+"F0.wireOp",EDGE,"E4"),sQuery(id+"F0.wireOp",EDGE,"E5"),sQuery(id+"F0.wireOp",EDGE,"E6"),sQuery(id+"F0.wireOp",EDGE,"E8"),sQuery(id+"F0.wireOp",EDGE,"E9")])],"isStart":false})]});
            var Q20;
            Q20=makeQuery(id+"F12.opFillet","BLEND_EDGE",EDGE,{"blendedFrom":[makeQuery(id+"F3.opExtrude","SWEPT_EDGE",EDGE,{"disambiguationData":[OSD([sQuery(id+"F2.wireOp",EDGE,"E148.MirrorCS"),sQuery(id+"F2.wireOp",EDGE,"E152.MirrorCS")])]}),makeQuery(id+"F1.opExtrude","CAP_FACE",FACE,{"disambiguationData":[OSD([sQuery(id+"F0.wireOp",EDGE,"E0.bottom"),sQuery(id+"F0.wireOp",EDGE,"E0.left"),sQuery(id+"F0.wireOp",EDGE,"E0.right"),sQuery(id+"F0.wireOp",EDGE,"E1.top"),sQuery(id+"F0.wireOp",EDGE,"E1.left"),sQuery(id+"F0.wireOp",EDGE,"E1.right"),sQuery(id+"F0.wireOp",EDGE,"E2"),sQuery(id+"F0.wireOp",EDGE,"E3"),sQuery(id+"F0.wireOp",EDGE,"E4"),sQuery(id+"F0.wireOp",EDGE,"E5"),sQuery(id+"F0.wireOp",EDGE,"E6"),sQuery(id+"F0.wireOp",EDGE,"E8"),sQuery(id+"F0.wireOp",EDGE,"E9")])],"isStart":false})],"blendedInto":[makeQuery(id+"F1.opExtrude","CAP_FACE",FACE,{"disambiguationData":[OSD([sQuery(id+"F0.wireOp",EDGE,"E0.bottom"),sQuery(id+"F0.wireOp",EDGE,"E0.left"),sQuery(id+"F0.wireOp",EDGE,"E0.right"),sQuery(id+"F0.wireOp",EDGE,"E1.top"),sQuery(id+"F0.wireOp",EDGE,"E1.left"),sQuery(id+"F0.wireOp",EDGE,"E1.right"),sQuery(id+"F0.wireOp",EDGE,"E2"),sQuery(id+"F0.wireOp",EDGE,"E3"),sQuery(id+"F0.wireOp",EDGE,"E4"),sQuery(id+"F0.wireOp",EDGE,"E5"),sQuery(id+"F0.wireOp",EDGE,"E6"),sQuery(id+"F0.wireOp",EDGE,"E8"),sQuery(id+"F0.wireOp",EDGE,"E9")])],"isStart":false})]});
            chamfer(context, id + "F15", {"entities" : qUnion([Q0, Q1, Q2, Q3, Q4, Q5, Q6, Q7, Q8, Q9, Q10, Q11, Q12, Q13, Q14, Q15, Q16, Q17, Q18, Q19, Q20]), "width" : 0.5 * mm, "tangentPropagation" : true});
        }
    });
